# Revit family: RN 92005 Optifitt-Serra-Raccordo
name_source: partatom
category: Rohrformteile
units: mm (PartAtom-declared; Revit-internal decimal feet)

## family parameters
Arbeitsebenenbasiert = Nein
Beim Laden mit Abzugskörper schneiden = Nein
Bemaßung runder Anschluss = Durchmesser verwenden
Gemeinsam genutzt = Nein
Immer vertikal = Ja
Teiletyp = Verbindung

## types (15) — shared parameters
1.010.00.2 Blattnummer der Richtlinie = 29
1.010.00.3 Ausgabedatum (Monat) der Richtlinie = 201308
1.010.00.4 Herstellername = R. Nussbaum AG
1.010.00.5 Revisionsdatum der Datei = 20190521
1.010.00.6 Webadresse des Herstellers = http://www.nussbaum.ch
1.100.00.4 Produktbezeichnung = Versorgung
1.110.00.2 Index = 3
1.110.00.4 Produktbezeichnung = Optifitt-Serra
1.960/3L.00.8 Link (URL) = https://www.nussbaum.ch
29.700.00.4 Produktname = Optifitt-Serra-Anschlussverschraubung, mit Innengewinde
29.700.00.5 Produktkennung = 2
29.700.00.6 Querschnittsform = 1
29.700.00.7 Nennweitensystem = DN
29.700.00.8 Nenndrucksystem = PN
29.710.02.4 Nenndruck = 16
29.710.02.5 max. zul. Überdruck [hPa] = 1600
29.710.02.7 max. zul. Dauer-Betriebsdruck [hPa] = 1600
29.710.02.9 max. zul. Dauer-Betriebstemperatur [°C] = 90
Connector Visibility = Nein
EnclosingSpace Visibility = Nein
R. Nussbaum AG 92005.26 de Visibility = Nein

## per-type parameters (varying)
- DN=65: 1.800.00.3 TGA-Nummer=01900300000000000000000000000000000000000000000039000000000000000016; 1.800.00.4 Kommentarfeld=92005.30, Optifitt-Serra-Anschlussverschraubung, mit Innengewinde, DN=65, L=39, Rp=2½; 1.810.00.3 Hersteller-Bestellnummer=92005.3; 1.810.00.4 DATANORM-Nummer=92005.3; 1.810.00.5 StLB-Nummer=671.141; 1.810.00.6 GTIN-Nummer=7612945037121; 29.710.02.10 Formstück-Gewicht [kg]=1.118; 29.710.02.3 Benennung=Optifitt-Serra-Anschlussverschraubung, mit Innengewinde, DN=65, L=39, Rp=2½; CONNECTOR0_DIAMETER_dX_0r=65 mm; CONNECTOR0_dX_01=27 mm  [stored 0.0885827 ft]; CONNECTOR0_ref_dX=27 mm  [stored 0.0885827 ft]; CONNECTOR1_DIAMETER_dX_0r=80 mm; CONNECTOR1_dX_00=39 mm  [stored 0.127953 ft]; CONNECTOR1_dX_01=55 mm; CONNECTOR1_ref_dX=39 mm  [stored 0.127953 ft]; Hersteller=R. Nussbaum AG; Modell=92005.3; R. Nussbaum AG 92005.21 de Visibility=Nein; R. Nussbaum AG 92005.22 de Visibility=Nein; R. Nussbaum AG 92005.23 de Visibility=Nein; R. Nussbaum AG 92005.24 de Visibility=Nein; R. Nussbaum AG 92005.25 de Visibility=Nein; R. Nussbaum AG 92005.27 de Visibility=Nein; R. Nussbaum AG 92005.28 de Visibility=Nein; R. Nussbaum AG 92005.29 de Visibility=Nein; R. Nussbaum AG 92005.30 de Visibility=Ja; R. Nussbaum AG 92005.31 de Visibility=Nein; R. Nussbaum AG 92005.32 de Visibility=Nein; R. Nussbaum AG 92005.33 de Visibility=Nein; R. Nussbaum AG 92005.34 de Visibility=Nein; R. Nussbaum AG 92005.35 de Visibility=Nein; R. Nussbaum AG 92005.36 de Visibility=Nein; Typenkommentare=Optifitt-Serra-Raccordo  DN=65; URL=https://www.nussbaum.ch
- DN=6: 1.800.00.3 TGA-Nummer=01900300000000000000000000000000000000000000000039000000000000000015; 1.800.00.4 Kommentarfeld=92005.36, Optifitt-Serra-Anschlussverschraubung, mit Innengewinde, DN=65, L=57, Rp=2½; 1.810.00.3 Hersteller-Bestellnummer=92005.36; 1.810.00.4 DATANORM-Nummer=92005.36; 1.810.00.6 GTIN-Nummer=7612945601834; 29.710.02.10 Formstück-Gewicht [kg]=1.119; 29.710.02.3 Benennung=Optifitt-Serra-Anschlussverschraubung, mit Innengewinde, DN=65, L=57, Rp=2½; CONNECTOR0_DIAMETER_dX_0r=65 mm; CONNECTOR0_dX_01=27 mm  [stored 0.0885827 ft]; CONNECTOR0_ref_dX=27 mm  [stored 0.0885827 ft]; CONNECTOR1_DIAMETER_dX_0r=80 mm; CONNECTOR1_dX_00=57 mm; CONNECTOR1_dX_01=72 mm; CONNECTOR1_ref_dX=57 mm; Hersteller=R. Nussbaum AG; Modell=92005.36; R. Nussbaum AG 92005.21 de Visibility=Nein; R. Nussbaum AG 92005.22 de Visibility=Nein; R. Nussbaum AG 92005.23 de Visibility=Nein; R. Nussbaum AG 92005.24 de Visibility=Nein; R. Nussbaum AG 92005.25 de Visibility=Nein; R. Nussbaum AG 92005.27 de Visibility=Nein; R. Nussbaum AG 92005.28 de Visibility=Nein; R. Nussbaum AG 92005.29 de Visibility=Nein; R. Nussbaum AG 92005.30 de Visibility=Nein; R. Nussbaum AG 92005.31 de Visibility=Nein; R. Nussbaum AG 92005.32 de Visibility=Nein; R. Nussbaum AG 92005.33 de Visibility=Nein; R. Nussbaum AG 92005.34 de Visibility=Nein; R. Nussbaum AG 92005.35 de Visibility=Nein; R. Nussbaum AG 92005.36 de Visibility=Ja; Typenkommentare=Optifitt-Serra-Raccordo  DN=65; URL=https://www.nussbaum.ch
- DN=50: 1.800.00.3 TGA-Nummer=01900300000000000000000000000000000000000000000039000000000000000014; 1.800.00.4 Kommentarfeld=92005.35, Optifitt-Serra-Anschlussverschraubung, mit Innengewinde, DN=50, L=52, Rp=2; 1.810.00.3 Hersteller-Bestellnummer=92005.35; 1.810.00.4 DATANORM-Nummer=92005.35; 1.810.00.6 GTIN-Nummer=7612945601827; 29.710.02.10 Formstück-Gewicht [kg]=0.767; 29.710.02.3 Benennung=Optifitt-Serra-Anschlussverschraubung, mit Innengewinde, DN=50, L=52, Rp=2; CONNECTOR0_DIAMETER_dX_0r=40 mm; CONNECTOR0_dX_01=19 mm; CONNECTOR0_ref_dX=19 mm; CONNECTOR1_DIAMETER_dX_0r=50 mm; CONNECTOR1_dX_00=52 mm; CONNECTOR1_dX_01=64 mm; CONNECTOR1_ref_dX=52 mm; Hersteller=R. Nussbaum AG; Modell=92005.35; R. Nussbaum AG 92005.21 de Visibility=Nein; R. Nussbaum AG 92005.22 de Visibility=Nein; R. Nussbaum AG 92005.23 de Visibility=Nein; R. Nussbaum AG 92005.24 de Visibility=Nein; R. Nussbaum AG 92005.25 de Visibility=Nein; R. Nussbaum AG 92005.27 de Visibility=Nein; R. Nussbaum AG 92005.28 de Visibility=Nein; R. Nussbaum AG 92005.29 de Visibility=Nein; R. Nussbaum AG 92005.30 de Visibility=Nein; R. Nussbaum AG 92005.31 de Visibility=Nein; R. Nussbaum AG 92005.32 de Visibility=Nein; R. Nussbaum AG 92005.33 de Visibility=Nein; R. Nussbaum AG 92005.34 de Visibility=Nein; R. Nussbaum AG 92005.35 de Visibility=Ja; R. Nussbaum AG 92005.36 de Visibility=Nein; Typenkommentare=Optifitt-Serra-Raccordo  DN=50; URL=https://www.nussbaum.ch
- DN=40: 1.800.00.3 TGA-Nummer=01900300000000000000000000000000000000000000000039000000000000000013; 1.800.00.4 Kommentarfeld=92005.34, Optifitt-Serra-Anschlussverschraubung, mit Innengewinde, DN=40, L=29, Rp=1½; 1.810.00.3 Hersteller-Bestellnummer=92005.34; 1.810.00.4 DATANORM-Nummer=92005.34; 1.810.00.6 GTIN-Nummer=7612945601919; 29.710.02.10 Formstück-Gewicht [kg]=0.512; 29.710.02.3 Benennung=Optifitt-Serra-Anschlussverschraubung, mit Innengewinde, DN=40, L=29, Rp=1½; CONNECTOR0_DIAMETER_dX_0r=40 mm; CONNECTOR0_dX_01=19 mm; CONNECTOR0_ref_dX=19 mm; CONNECTOR1_DIAMETER_dX_0r=50 mm; CONNECTOR1_dX_00=29 mm; CONNECTOR1_dX_01=44 mm; CONNECTOR1_ref_dX=29 mm; Hersteller=R. Nussbaum AG; Modell=92005.34; R. Nussbaum AG 92005.21 de Visibility=Nein; R. Nussbaum AG 92005.22 de Visibility=Nein; R. Nussbaum AG 92005.23 de Visibility=Nein; R. Nussbaum AG 92005.24 de Visibility=Nein; R. Nussbaum AG 92005.25 de Visibility=Nein; R. Nussbaum AG 92005.27 de Visibility=Nein; R. Nussbaum AG 92005.28 de Visibility=Nein; R. Nussbaum AG 92005.29 de Visibility=Nein; R. Nussbaum AG 92005.30 de Visibility=Nein; R. Nussbaum AG 92005.31 de Visibility=Nein; R. Nussbaum AG 92005.32 de Visibility=Nein; R. Nussbaum AG 92005.33 de Visibility=Nein; R. Nussbaum AG 92005.34 de Visibility=Ja; R. Nussbaum AG 92005.35 de Visibility=Nein; R. Nussbaum AG 92005.36 de Visibility=Nein; Typenkommentare=Optifitt-Serra-Raccordo  DN=40; URL=https://www.nussbaum.ch
- DN=5: 1.800.00.3 TGA-Nummer=01900300000000000000000000000000000000000000000039000000000000000012; 1.800.00.4 Kommentarfeld=92005.33, Optifitt-Serra-Anschlussverschraubung, mit Innengewinde, DN=40, L=46, Rp=1½; 1.810.00.3 Hersteller-Bestellnummer=92005.33; 1.810.00.4 DATANORM-Nummer=92005.33; 1.810.00.6 GTIN-Nummer=7612945601810; 29.710.02.10 Formstück-Gewicht [kg]=0.426; 29.710.02.3 Benennung=Optifitt-Serra-Anschlussverschraubung, mit Innengewinde, DN=40, L=46, Rp=1½; CONNECTOR0_DIAMETER_dX_0r=40 mm; CONNECTOR0_dX_01=19 mm; CONNECTOR0_ref_dX=19 mm; CONNECTOR1_DIAMETER_dX_0r=40 mm; CONNECTOR1_dX_00=46 mm; CONNECTOR1_dX_01=57 mm; CONNECTOR1_ref_dX=46 mm; Hersteller=R. Nussbaum AG; Modell=92005.33; R. Nussbaum AG 92005.21 de Visibility=Nein; R. Nussbaum AG 92005.22 de Visibility=Nein; R. Nussbaum AG 92005.23 de Visibility=Nein; R. Nussbaum AG 92005.24 de Visibility=Nein; R. Nussbaum AG 92005.25 de Visibility=Nein; R. Nussbaum AG 92005.27 de Visibility=Nein; R. Nussbaum AG 92005.28 de Visibility=Nein; R. Nussbaum AG 92005.29 de Visibility=Nein; R. Nussbaum AG 92005.30 de Visibility=Nein; R. Nussbaum AG 92005.31 de Visibility=Nein; R. Nussbaum AG 92005.32 de Visibility=Nein; R. Nussbaum AG 92005.33 de Visibility=Ja; R. Nussbaum AG 92005.34 de Visibility=Nein; R. Nussbaum AG 92005.35 de Visibility=Nein; R. Nussbaum AG 92005.36 de Visibility=Nein; Typenkommentare=Optifitt-Serra-Raccordo  DN=40; URL=https://www.nussbaum.ch
- DN=2: 1.800.00.3 TGA-Nummer=01900300000000000000000000000000000000000000000039000000000000000011; 1.800.00.4 Kommentarfeld=92005.32, Optifitt-Serra-Anschlussverschraubung, mit Innengewinde, DN=32, L=47, Rp=1¼; 1.810.00.3 Hersteller-Bestellnummer=92005.32; 1.810.00.4 DATANORM-Nummer=92005.32; 1.810.00.6 GTIN-Nummer=7612945601803; 29.710.02.10 Formstück-Gewicht [kg]=0.323; 29.710.02.3 Benennung=Optifitt-Serra-Anschlussverschraubung, mit Innengewinde, DN=32, L=47, Rp=1¼; CONNECTOR0_DIAMETER_dX_0r=32 mm  [stored 0.104987 ft]; CONNECTOR0_dX_01=19 mm; CONNECTOR0_ref_dX=19 mm; CONNECTOR1_DIAMETER_dX_0r=40 mm; CONNECTOR1_dX_00=47 mm; CONNECTOR1_dX_01=58 mm; CONNECTOR1_ref_dX=47 mm; Hersteller=R. Nussbaum AG; Modell=92005.32; R. Nussbaum AG 92005.21 de Visibility=Nein; R. Nussbaum AG 92005.22 de Visibility=Nein; R. Nussbaum AG 92005.23 de Visibility=Nein; R. Nussbaum AG 92005.24 de Visibility=Nein; R. Nussbaum AG 92005.25 de Visibility=Nein; R. Nussbaum AG 92005.27 de Visibility=Nein; R. Nussbaum AG 92005.28 de Visibility=Nein; R. Nussbaum AG 92005.29 de Visibility=Nein; R. Nussbaum AG 92005.30 de Visibility=Nein; R. Nussbaum AG 92005.31 de Visibility=Nein; R. Nussbaum AG 92005.32 de Visibility=Ja; R. Nussbaum AG 92005.33 de Visibility=Nein; R. Nussbaum AG 92005.34 de Visibility=Nein; R. Nussbaum AG 92005.35 de Visibility=Nein; R. Nussbaum AG 92005.36 de Visibility=Nein; Typenkommentare=Optifitt-Serra-Raccordo  DN=32; URL=https://www.nussbaum.ch
- DN=1: 1.800.00.3 TGA-Nummer=01900300000000000000000000000000000000000000000039000000000000000010; 1.800.00.4 Kommentarfeld=92005.31, Optifitt-Serra-Anschlussverschraubung, mit Innengewinde, DN=25, L=40, Rp=1; 1.810.00.3 Hersteller-Bestellnummer=92005.31; 1.810.00.4 DATANORM-Nummer=92005.31; 1.810.00.6 GTIN-Nummer=7612945601797; 29.710.02.10 Formstück-Gewicht [kg]=0.239; 29.710.02.3 Benennung=Optifitt-Serra-Anschlussverschraubung, mit Innengewinde, DN=25, L=40, Rp=1; CONNECTOR0_DIAMETER_dX_0r=25 mm  [stored 0.082021 ft]; CONNECTOR0_dX_01=17 mm; CONNECTOR0_ref_dX=17 mm; CONNECTOR1_DIAMETER_dX_0r=32 mm  [stored 0.104987 ft]; CONNECTOR1_dX_00=40 mm; CONNECTOR1_dX_01=51 mm; CONNECTOR1_ref_dX=40 mm; Hersteller=R. Nussbaum AG; Modell=92005.31; R. Nussbaum AG 92005.21 de Visibility=Nein; R. Nussbaum AG 92005.22 de Visibility=Nein; R. Nussbaum AG 92005.23 de Visibility=Nein; R. Nussbaum AG 92005.24 de Visibility=Nein; R. Nussbaum AG 92005.25 de Visibility=Nein; R. Nussbaum AG 92005.27 de Visibility=Nein; R. Nussbaum AG 92005.28 de Visibility=Nein; R. Nussbaum AG 92005.29 de Visibility=Nein; R. Nussbaum AG 92005.30 de Visibility=Nein; R. Nussbaum AG 92005.31 de Visibility=Ja; R. Nussbaum AG 92005.32 de Visibility=Nein; R. Nussbaum AG 92005.33 de Visibility=Nein; R. Nussbaum AG 92005.34 de Visibility=Nein; R. Nussbaum AG 92005.35 de Visibility=Nein; R. Nussbaum AG 92005.36 de Visibility=Nein; Typenkommentare=Optifitt-Serra-Raccordo  DN=25; URL=https://www.nussbaum.ch
- DN=4: 1.800.00.3 TGA-Nummer=01900300000000000000000000000000000000000000000039000000000000000009; 1.800.00.4 Kommentarfeld=92005.29, Optifitt-Serra-Anschlussverschraubung, mit Innengewinde, DN=50, L=37, Rp=2; 1.810.00.3 Hersteller-Bestellnummer=92005.29; 1.810.00.4 DATANORM-Nummer=92005.29; 1.810.00.5 StLB-Nummer=671.138; 1.810.00.6 GTIN-Nummer=7612945037114; 29.710.02.10 Formstück-Gewicht [kg]=0.703; 29.710.02.3 Benennung=Optifitt-Serra-Anschlussverschraubung, mit Innengewinde, DN=50, L=37, Rp=2; CONNECTOR0_DIAMETER_dX_0r=50 mm; CONNECTOR0_dX_01=24 mm; CONNECTOR0_ref_dX=24 mm; CONNECTOR1_DIAMETER_dX_0r=65 mm; CONNECTOR1_dX_00=37 mm; CONNECTOR1_dX_01=57 mm; CONNECTOR1_ref_dX=37 mm; Hersteller=R. Nussbaum AG; Modell=92005.29; R. Nussbaum AG 92005.21 de Visibility=Nein; R. Nussbaum AG 92005.22 de Visibility=Nein; R. Nussbaum AG 92005.23 de Visibility=Nein; R. Nussbaum AG 92005.24 de Visibility=Nein; R. Nussbaum AG 92005.25 de Visibility=Nein; R. Nussbaum AG 92005.27 de Visibility=Nein; R. Nussbaum AG 92005.28 de Visibility=Nein; R. Nussbaum AG 92005.29 de Visibility=Ja; R. Nussbaum AG 92005.30 de Visibility=Nein; R. Nussbaum AG 92005.31 de Visibility=Nein; R. Nussbaum AG 92005.32 de Visibility=Nein; R. Nussbaum AG 92005.33 de Visibility=Nein; R. Nussbaum AG 92005.34 de Visibility=Nein; R. Nussbaum AG 92005.35 de Visibility=Nein; R. Nussbaum AG 92005.36 de Visibility=Nein; Typenkommentare=Optifitt-Serra-Raccordo  DN=50; URL=https://www.nussbaum.ch
- DN=3: 1.800.00.3 TGA-Nummer=01900300000000000000000000000000000000000000000039000000000000000008; 1.800.00.4 Kommentarfeld=92005.28, Optifitt-Serra-Anschlussverschraubung, mit Innengewinde, DN=40, L=35, Rp=1½; 1.810.00.3 Hersteller-Bestellnummer=92005.28; 1.810.00.4 DATANORM-Nummer=92005.28; 1.810.00.5 StLB-Nummer=671.137; 1.810.00.6 GTIN-Nummer=7612945037107; 29.710.02.10 Formstück-Gewicht [kg]=0.456; 29.710.02.3 Benennung=Optifitt-Serra-Anschlussverschraubung, mit Innengewinde, DN=40, L=35, Rp=1½; CONNECTOR0_DIAMETER_dX_0r=40 mm; CONNECTOR0_dX_01=19 mm; CONNECTOR0_ref_dX=19 mm; CONNECTOR1_DIAMETER_dX_0r=40 mm; CONNECTOR1_dX_00=35 mm; CONNECTOR1_dX_01=52 mm; CONNECTOR1_ref_dX=35 mm; Hersteller=R. Nussbaum AG; Modell=92005.28; R. Nussbaum AG 92005.21 de Visibility=Nein; R. Nussbaum AG 92005.22 de Visibility=Nein; R. Nussbaum AG 92005.23 de Visibility=Nein; R. Nussbaum AG 92005.24 de Visibility=Nein; R. Nussbaum AG 92005.25 de Visibility=Nein; R. Nussbaum AG 92005.27 de Visibility=Nein; R. Nussbaum AG 92005.28 de Visibility=Ja; R. Nussbaum AG 92005.29 de Visibility=Nein; R. Nussbaum AG 92005.30 de Visibility=Nein; R. Nussbaum AG 92005.31 de Visibility=Nein; R. Nussbaum AG 92005.32 de Visibility=Nein; R. Nussbaum AG 92005.33 de Visibility=Nein; R. Nussbaum AG 92005.34 de Visibility=Nein; R. Nussbaum AG 92005.35 de Visibility=Nein; R. Nussbaum AG 92005.36 de Visibility=Nein; Typenkommentare=Optifitt-Serra-Raccordo  DN=40; URL=https://www.nussbaum.ch
- DN=32: 1.800.00.3 TGA-Nummer=01900300000000000000000000000000000000000000000039000000000000000007; 1.800.00.4 Kommentarfeld=92005.27, Optifitt-Serra-Anschlussverschraubung, mit Innengewinde, DN=32, L=33, Rp=1¼; 1.810.00.3 Hersteller-Bestellnummer=92005.27; 1.810.00.4 DATANORM-Nummer=92005.27; 1.810.00.5 StLB-Nummer=671.136; 1.810.00.6 GTIN-Nummer=7612945037091; 29.710.02.10 Formstück-Gewicht [kg]=0.431; 29.710.02.3 Benennung=Optifitt-Serra-Anschlussverschraubung, mit Innengewinde, DN=32, L=33, Rp=1¼; CONNECTOR0_DIAMETER_dX_0r=32 mm  [stored 0.104987 ft]; CONNECTOR0_dX_01=19 mm; CONNECTOR0_ref_dX=19 mm; CONNECTOR1_DIAMETER_dX_0r=50 mm; CONNECTOR1_dX_00=48 mm; CONNECTOR1_dX_01=62 mm; CONNECTOR1_ref_dX=62 mm; R. Nussbaum AG 92005.21 de Visibility=Nein; R. Nussbaum AG 92005.22 de Visibility=Nein; R. Nussbaum AG 92005.23 de Visibility=Nein; R. Nussbaum AG 92005.24 de Visibility=Nein; R. Nussbaum AG 92005.25 de Visibility=Nein; R. Nussbaum AG 92005.27 de Visibility=Ja; R. Nussbaum AG 92005.28 de Visibility=Nein; R. Nussbaum AG 92005.29 de Visibility=Nein; R. Nussbaum AG 92005.30 de Visibility=Nein; R. Nussbaum AG 92005.31 de Visibility=Nein; R. Nussbaum AG 92005.32 de Visibility=Nein; R. Nussbaum AG 92005.33 de Visibility=Nein; R. Nussbaum AG 92005.34 de Visibility=Nein; R. Nussbaum AG 92005.35 de Visibility=Nein; R. Nussbaum AG 92005.36 de Visibility=Nein
- DN=25: 1.800.00.3 TGA-Nummer=01900300000000000000000000000000000000000000000039000000000000000005; 1.800.00.4 Kommentarfeld=92005.25, Optifitt-Serra-Anschlussverschraubung, mit Innengewinde, DN=25, L=28, Rp=1; 1.810.00.3 Hersteller-Bestellnummer=92005.25; 1.810.00.4 DATANORM-Nummer=92005.25; 1.810.00.5 StLB-Nummer=671.135; 1.810.00.6 GTIN-Nummer=7612945037077; 29.710.02.10 Formstück-Gewicht [kg]=0.218; 29.710.02.3 Benennung=Optifitt-Serra-Anschlussverschraubung, mit Innengewinde, DN=25, L=28, Rp=1; CONNECTOR0_DIAMETER_dX_0r=25 mm  [stored 0.082021 ft]; CONNECTOR0_dX_01=17 mm; CONNECTOR0_ref_dX=17 mm; CONNECTOR1_DIAMETER_dX_0r=40 mm; CONNECTOR1_dX_00=28 mm; CONNECTOR1_dX_01=38 mm  [stored 0.124672 ft]; CONNECTOR1_ref_dX=28 mm; R. Nussbaum AG 92005.21 de Visibility=Nein; R. Nussbaum AG 92005.22 de Visibility=Nein; R. Nussbaum AG 92005.23 de Visibility=Nein; R. Nussbaum AG 92005.24 de Visibility=Nein; R. Nussbaum AG 92005.25 de Visibility=Ja; R. Nussbaum AG 92005.27 de Visibility=Nein; R. Nussbaum AG 92005.28 de Visibility=Nein; R. Nussbaum AG 92005.29 de Visibility=Nein; R. Nussbaum AG 92005.30 de Visibility=Nein; R. Nussbaum AG 92005.31 de Visibility=Nein; R. Nussbaum AG 92005.32 de Visibility=Nein; R. Nussbaum AG 92005.33 de Visibility=Nein; R. Nussbaum AG 92005.34 de Visibility=Nein; R. Nussbaum AG 92005.35 de Visibility=Nein; R. Nussbaum AG 92005.36 de Visibility=Nein
- DN=20: 1.800.00.3 TGA-Nummer=01900300000000000000000000000000000000000000000039000000000000000004; 1.800.00.4 Kommentarfeld=92005.24, Optifitt-Serra-Anschlussverschraubung, mit Innengewinde, DN=20, L=27, Rp=¾; 1.810.00.3 Hersteller-Bestellnummer=92005.24; 1.810.00.4 DATANORM-Nummer=92005.24; 1.810.00.6 GTIN-Nummer=7612945037060; 29.710.02.10 Formstück-Gewicht [kg]=0.227; 29.710.02.3 Benennung=Optifitt-Serra-Anschlussverschraubung, mit Innengewinde, DN=20, L=27, Rp=¾; CONNECTOR0_DIAMETER_dX_0r=20 mm; CONNECTOR0_dX_01=15 mm  [stored 0.0492126 ft]; CONNECTOR0_ref_dX=15 mm  [stored 0.0492126 ft]; CONNECTOR1_DIAMETER_dX_0r=40 mm; CONNECTOR1_dX_00=38 mm  [stored 0.124672 ft]; CONNECTOR1_dX_01=48 mm; CONNECTOR1_ref_dX=48 mm; R. Nussbaum AG 92005.21 de Visibility=Nein; R. Nussbaum AG 92005.22 de Visibility=Nein; R. Nussbaum AG 92005.23 de Visibility=Nein; R. Nussbaum AG 92005.24 de Visibility=Ja; R. Nussbaum AG 92005.25 de Visibility=Nein; R. Nussbaum AG 92005.27 de Visibility=Nein; R. Nussbaum AG 92005.28 de Visibility=Nein; R. Nussbaum AG 92005.29 de Visibility=Nein; R. Nussbaum AG 92005.30 de Visibility=Nein; R. Nussbaum AG 92005.31 de Visibility=Nein; R. Nussbaum AG 92005.32 de Visibility=Nein; R. Nussbaum AG 92005.33 de Visibility=Nein; R. Nussbaum AG 92005.34 de Visibility=Nein; R. Nussbaum AG 92005.35 de Visibility=Nein; R. Nussbaum AG 92005.36 de Visibility=Nein
- DN=8: 1.800.00.3 TGA-Nummer=01900300000000000000000000000000000000000000000039000000000000000003; 1.800.00.4 Kommentarfeld=92005.23, Optifitt-Serra-Anschlussverschraubung, mit Innengewinde, DN=20, L=25, Rp=¾; 1.810.00.3 Hersteller-Bestellnummer=92005.23; 1.810.00.4 DATANORM-Nummer=92005.23; 1.810.00.5 StLB-Nummer=671.134; 1.810.00.6 GTIN-Nummer=7612945037053; 29.710.02.10 Formstück-Gewicht [kg]=0.177; 29.710.02.3 Benennung=Optifitt-Serra-Anschlussverschraubung, mit Innengewinde, DN=20, L=25, Rp=¾; CONNECTOR0_DIAMETER_dX_0r=20 mm; CONNECTOR0_dX_01=15 mm  [stored 0.0492126 ft]; CONNECTOR0_ref_dX=15 mm  [stored 0.0492126 ft]; CONNECTOR1_DIAMETER_dX_0r=32 mm  [stored 0.104987 ft]; CONNECTOR1_dX_00=25 mm  [stored 0.082021 ft]; CONNECTOR1_dX_01=35 mm; CONNECTOR1_ref_dX=25 mm  [stored 0.082021 ft]; Hersteller=R. Nussbaum AG; Modell=92005.23; R. Nussbaum AG 92005.21 de Visibility=Nein; R. Nussbaum AG 92005.22 de Visibility=Nein; R. Nussbaum AG 92005.23 de Visibility=Ja; R. Nussbaum AG 92005.24 de Visibility=Nein; R. Nussbaum AG 92005.25 de Visibility=Nein; R. Nussbaum AG 92005.27 de Visibility=Nein; R. Nussbaum AG 92005.28 de Visibility=Nein; R. Nussbaum AG 92005.29 de Visibility=Nein; R. Nussbaum AG 92005.30 de Visibility=Nein; R. Nussbaum AG 92005.31 de Visibility=Nein; R. Nussbaum AG 92005.32 de Visibility=Nein; R. Nussbaum AG 92005.33 de Visibility=Nein; R. Nussbaum AG 92005.34 de Visibility=Nein; R. Nussbaum AG 92005.35 de Visibility=Nein; R. Nussbaum AG 92005.36 de Visibility=Nein; Typenkommentare=Optifitt-Serra-Raccordo  DN=20; URL=https://www.nussbaum.ch
- DN=7: 1.800.00.3 TGA-Nummer=01900300000000000000000000000000000000000000000039000000000000000002; 1.800.00.4 Kommentarfeld=92005.22, Optifitt-Serra-Anschlussverschraubung, mit Innengewinde, DN=15, L=23, Rp=½; 1.810.00.3 Hersteller-Bestellnummer=92005.22; 1.810.00.4 DATANORM-Nummer=92005.22; 1.810.00.6 GTIN-Nummer=7612945037046; 29.710.02.10 Formstück-Gewicht [kg]=0.215; 29.710.02.3 Benennung=Optifitt-Serra-Anschlussverschraubung, mit Innengewinde, DN=15, L=23, Rp=½; CONNECTOR0_DIAMETER_dX_0r=15 mm  [stored 0.0492126 ft]; CONNECTOR0_dX_01=13 mm  [stored 0.0426509 ft]; CONNECTOR0_ref_dX=13 mm  [stored 0.0426509 ft]; CONNECTOR1_DIAMETER_dX_0r=40 mm; CONNECTOR1_dX_00=23 mm  [stored 0.0754593 ft]; CONNECTOR1_dX_01=33 mm  [stored 0.108268 ft]; CONNECTOR1_ref_dX=23 mm  [stored 0.0754593 ft]; Hersteller=R. Nussbaum AG; Modell=92005.22; R. Nussbaum AG 92005.21 de Visibility=Nein; R. Nussbaum AG 92005.22 de Visibility=Ja; R. Nussbaum AG 92005.23 de Visibility=Nein; R. Nussbaum AG 92005.24 de Visibility=Nein; R. Nussbaum AG 92005.25 de Visibility=Nein; R. Nussbaum AG 92005.27 de Visibility=Nein; R. Nussbaum AG 92005.28 de Visibility=Nein; R. Nussbaum AG 92005.29 de Visibility=Nein; R. Nussbaum AG 92005.30 de Visibility=Nein; R. Nussbaum AG 92005.31 de Visibility=Nein; R. Nussbaum AG 92005.32 de Visibility=Nein; R. Nussbaum AG 92005.33 de Visibility=Nein; R. Nussbaum AG 92005.34 de Visibility=Nein; R. Nussbaum AG 92005.35 de Visibility=Nein; R. Nussbaum AG 92005.36 de Visibility=Nein; Typenkommentare=Optifitt-Serra-Raccordo  DN=15; URL=https://www.nussbaum.ch
- DN=15: 1.800.00.3 TGA-Nummer=01900300000000000000000000000000000000000000000039000000000000000001; 1.800.00.4 Kommentarfeld=92005.21, Optifitt-Serra-Anschlussverschraubung, mit Innengewinde, DN=15, L=23, Rp=½; 1.810.00.3 Hersteller-Bestellnummer=92005.21; 1.810.00.4 DATANORM-Nummer=92005.21; 1.810.00.5 StLB-Nummer=671.133; 1.810.00.6 GTIN-Nummer=7612945037039; 29.710.02.10 Formstück-Gewicht [kg]=0.153; 29.710.02.3 Benennung=Optifitt-Serra-Anschlussverschraubung, mit Innengewinde, DN=15, L=23, Rp=½; CONNECTOR0_DIAMETER_dX_0r=15 mm  [stored 0.0492126 ft]; CONNECTOR0_dX_01=13 mm  [stored 0.0426509 ft]; CONNECTOR0_ref_dX=13 mm  [stored 0.0426509 ft]; CONNECTOR1_DIAMETER_dX_0r=25 mm  [stored 0.082021 ft]; CONNECTOR1_dX_00=23 mm  [stored 0.0754593 ft]; CONNECTOR1_dX_01=34 mm; CONNECTOR1_ref_dX=23 mm  [stored 0.0754593 ft]; R. Nussbaum AG 92005.21 de Visibility=Ja; R. Nussbaum AG 92005.22 de Visibility=Nein; R. Nussbaum AG 92005.23 de Visibility=Nein; R. Nussbaum AG 92005.24 de Visibility=Nein; R. Nussbaum AG 92005.25 de Visibility=Nein; R. Nussbaum AG 92005.27 de Visibility=Nein; R. Nussbaum AG 92005.28 de Visibility=Nein; R. Nussbaum AG 92005.29 de Visibility=Nein; R. Nussbaum AG 92005.30 de Visibility=Nein; R. Nussbaum AG 92005.31 de Visibility=Nein; R. Nussbaum AG 92005.32 de Visibility=Nein; R. Nussbaum AG 92005.33 de Visibility=Nein; R. Nussbaum AG 92005.34 de Visibility=Nein; R. Nussbaum AG 92005.35 de Visibility=Nein; R. Nussbaum AG 92005.36 de Visibility=Nein

note: [stored X ft] marks values corroborated as IEEE doubles in the binary element streams (Revit-internal decimal feet)

## geometry (parser evidence)
native form markers: Sweep x3
no freeform markers — native parametric forms only
